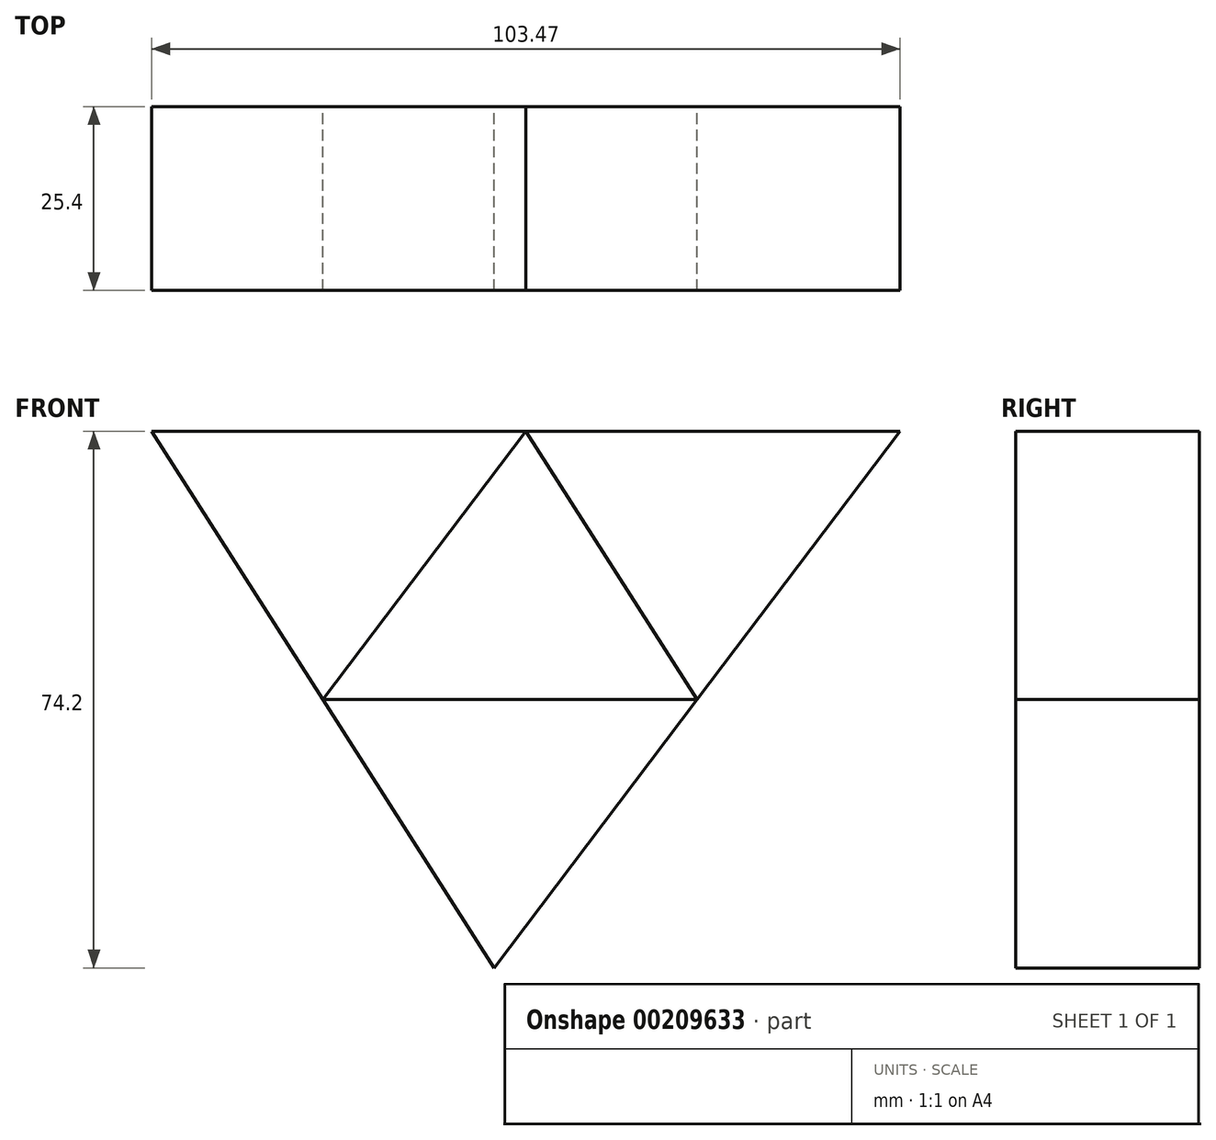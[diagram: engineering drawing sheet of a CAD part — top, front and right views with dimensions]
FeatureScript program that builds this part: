
annotation { "Feature Type Name" : "Feature", "Feature Type Description" : "" }
export const myFeature = defineFeature(function(context is Context, id is Id, definition is map)
    precondition{}
    {
        {
            var Q0;
            Q0=qCreatedBy(makeId("Front.planeOp"),FACE);
            var sketch = newSketch(context, id + "F0", { "sketchPlane" : qUnion([Q0])});
            skLineSegment(sketch, "E0", {"start": v(-56.15, 29.48) * mm, "end": v(47.32, 29.48) * mm});
            skLineSegment(sketch, "E1", {"start": v(47.32, 29.48) * mm, "end": v(-8.82, -44.72) * mm});
            skLineSegment(sketch, "E2", {"start": v(-8.82, -44.72) * mm, "end": v(-56.15, 29.48) * mm});
            skLineSegment(sketch, "E3", {"start": v(-32.49, -7.62) * mm, "end": v(19.25, -7.62) * mm});
            skLineSegment(sketch, "E4", {"start": v(19.25, -7.62) * mm, "end": v(-4.41, 29.48) * mm});
            skLineSegment(sketch, "E5", {"start": v(-4.41, 29.48) * mm, "end": v(-32.49, -7.62) * mm});
            skSolve(sketch);
        }
        {
            var Q0;
            {var subQ3=sQuery(id+"F0.wireOp",EDGE,"E3");Q0=makeQuery(id+"F0.imprint","IMPRINT",FACE,{"disambiguationData":[TD([[makeQuery(id+"F0.imprint","IMPRINT",EDGE,{"derivedFrom":subQ3}),-1.0]])]});}
            var Q1;
            {var subQ3=sQuery(id+"F0.wireOp",EDGE,"E5");Q1=makeQuery(id+"F0.imprint","IMPRINT",FACE,{"disambiguationData":[TD([[makeQuery(id+"F0.imprint","IMPRINT",EDGE,{"derivedFrom":subQ3}),-1.0]])]});}
            var Q2;
            {var subQ3=sQuery(id+"F0.wireOp",EDGE,"E4");Q2=makeQuery(id+"F0.imprint","IMPRINT",FACE,{"disambiguationData":[TD([[makeQuery(id+"F0.imprint","IMPRINT",EDGE,{"derivedFrom":subQ3}),-1.0]])]});}
            extrude(context, id + "F1", {"entities" : qUnion([Q0, Q1, Q2]), "depth" : 25.4 * mm});
        }
    });
